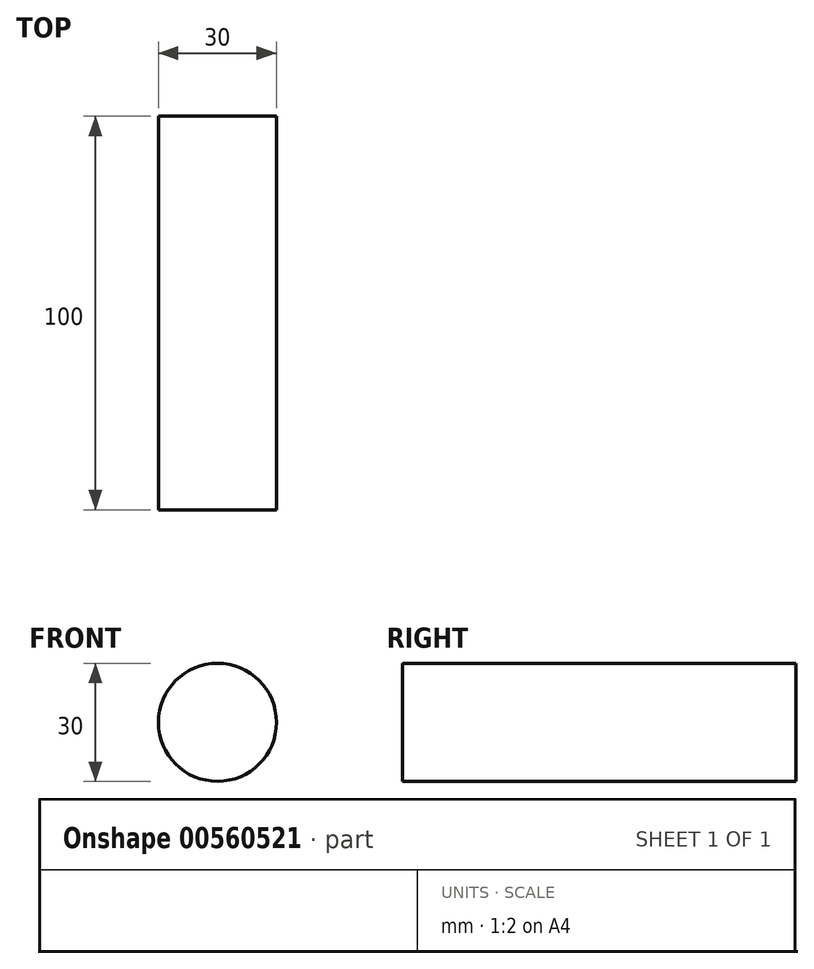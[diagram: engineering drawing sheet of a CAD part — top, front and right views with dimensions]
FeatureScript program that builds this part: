
annotation { "Feature Type Name" : "Feature", "Feature Type Description" : "" }
export const myFeature = defineFeature(function(context is Context, id is Id, definition is map)
    precondition{}
    {
        {
            var Q0;
            Q0=qCreatedBy(makeId("Front.planeOp"),FACE);
            var sketch = newSketch(context, id + "F0", { "sketchPlane" : qUnion([Q0])});
            skCircle(sketch, "E0", {"center": v(0, 0) * mm, "radius": 15 * mm});
            skSolve(sketch);
        }
        {
            var Q0;
            Q0=makeQuery(id+"F0.imprint","IMPRINT",FACE,{"disambiguationData":[TD([[makeQuery(id+"F0.imprint","IMPRINT",EDGE,{"derivedFrom":sQuery(id+"F0.wireOp",EDGE,"E0")}),1.0]])]});
            extrude(context, id + "F1", {"entities" : qUnion([Q0]), "depth" : 100 * mm, "offsetDistance" : 25 * mm});
        }
    });
